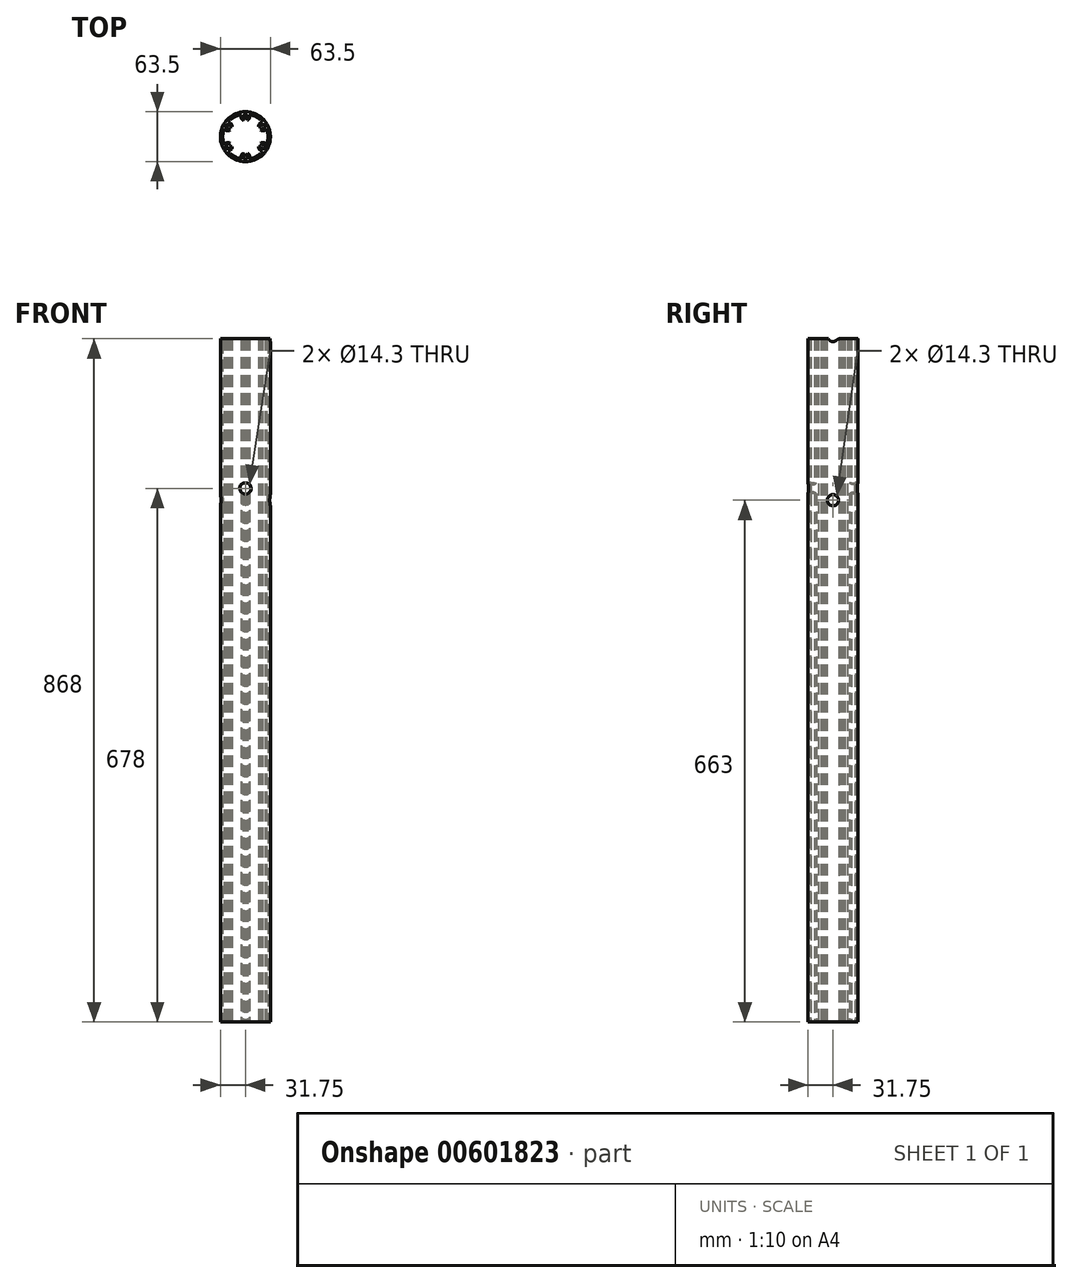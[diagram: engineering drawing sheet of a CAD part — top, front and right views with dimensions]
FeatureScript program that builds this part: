
annotation { "Feature Type Name" : "Feature", "Feature Type Description" : "" }
export const myFeature = defineFeature(function(context is Context, id is Id, definition is map)
    precondition{}
    {
        {
            var Q0;
            Q0=qCreatedBy(makeId("Top.planeOp"),FACE);
            var sketch = newSketch(context, id + "F0", { "sketchPlane" : qUnion([Q0])});
            skCircle(sketch, "E0", {"center": v(0, 0) * mm, "radius": 31.75 * mm});
            skCircle(sketch, "E1", {"center": v(0, 0) * mm, "radius": 28.75 * mm});
            skSolve(sketch);
        }
        {
            var Q0;
            Q0 = qSketchRegion(id + "F0", true);
            extrude(context, id + "F1", {"entities" : qUnion([Q0]), "depth" : 868 * mm, "offsetDistance" : 25 * mm});
        }
        {
            var Q0;
            Q0=qCreatedBy(makeId("Top.planeOp"),FACE);
            var sketch = newSketch(context, id + "F2", { "sketchPlane" : qUnion([Q0])});
            skCircle(sketch, "E2", {"center": v(0, 0) * mm, "radius": 25.75 * mm, "construction": true});
            skPoint(sketch, "E3", {"position": v(0, 25.75) * mm});
            skCircle(sketch, "E4", {"center": v(0, 25.75) * mm, "radius": 2.5 * mm});
            skCircle(sketch, "E5", {"center": v(0, 25.75) * mm, "radius": 5.5 * mm});
            skCircle(sketch, "E6.1.0", {"center": v(-22.3, 12.88) * mm, "radius": 5.5 * mm});
            skCircle(sketch, "E6.1.1", {"center": v(-22.3, 12.88) * mm, "radius": 2.5 * mm});
            skCircle(sketch, "E6.2.0", {"center": v(-22.3, -12.87) * mm, "radius": 5.5 * mm});
            skCircle(sketch, "E6.2.1", {"center": v(-22.3, -12.87) * mm, "radius": 2.5 * mm});
            skCircle(sketch, "E6.3.0", {"center": v(0, -25.75) * mm, "radius": 5.5 * mm});
            skCircle(sketch, "E6.3.1", {"center": v(0, -25.75) * mm, "radius": 2.5 * mm});
            skCircle(sketch, "E6.4.0", {"center": v(22.3, -12.88) * mm, "radius": 5.5 * mm});
            skCircle(sketch, "E6.4.1", {"center": v(22.3, -12.88) * mm, "radius": 2.5 * mm});
            skCircle(sketch, "E6.5.0", {"center": v(22.3, 12.88) * mm, "radius": 5.5 * mm});
            skCircle(sketch, "E6.5.1", {"center": v(22.3, 12.88) * mm, "radius": 2.5 * mm});
            skSolve(sketch);
        }
        {
            var Q0;
            Q0 = qSketchRegion(id + "F2", true);
            var Q1;
            Q1=makeQuery(id+"F1.opExtrude","CAP_FACE",FACE,{"disambiguationData":[OSD([sQuery(id+"F0.wireOp",EDGE,"E0"),sQuery(id+"F0.wireOp",EDGE,"E1")])],"isStart":false});
            extrude(context, id + "F3", {"entities" : qUnion([Q0]), "operationType" : NewBodyOperationType.ADD, "endBound" : BoundingType.UP_TO_SURFACE, "depth" : 25 * mm, "endBoundEntityFace" : qUnion([Q1]), "offsetDistance" : 25 * mm});
        }
        {
            var Q0;
            Q0=qCreatedBy(makeId("Top.planeOp"),FACE);
            var sketch = newSketch(context, id + "F4", { "sketchPlane" : qUnion([Q0])});
            skPoint(sketch, "E7", {"position": v(0, 25.75) * mm});
            skPoint(sketch, "E8", {"position": v(0, 20.25) * mm});
            skArc(sketch, "E9", {"start": v(-2.75, 20.99) * mm, "mid": v(0, 20.25) * mm, "end": v(2.75, 20.99) * mm});
            skLineSegment(sketch, "E10", {"start": v(0, 25.75) * mm, "end": v(-2.75, 20.99) * mm});
            skLineSegment(sketch, "E11", {"start": v(0, 25.75) * mm, "end": v(2.75, 20.99) * mm});
            skLineSegment(sketch, "E12.1.0", {"start": v(-22.3, 12.88) * mm, "end": v(-19.55, 8.11) * mm});
            skLineSegment(sketch, "E12.1.1", {"start": v(-22.3, 12.88) * mm, "end": v(-16.8, 12.88) * mm});
            skArc(sketch, "E12.1.2", {"start": v(-19.55, 8.11) * mm, "mid": v(-17.54, 10.13) * mm, "end": v(-16.8, 12.87) * mm});
            skLineSegment(sketch, "E12.2.0", {"start": v(-22.3, -12.87) * mm, "end": v(-16.8, -12.87) * mm});
            skLineSegment(sketch, "E12.2.1", {"start": v(-22.3, -12.87) * mm, "end": v(-19.55, -8.11) * mm});
            skArc(sketch, "E12.2.2", {"start": v(-16.8, -12.87) * mm, "mid": v(-17.54, -10.12) * mm, "end": v(-19.55, -8.11) * mm});
            skLineSegment(sketch, "E12.3.0", {"start": v(0, -25.75) * mm, "end": v(2.75, -20.99) * mm});
            skLineSegment(sketch, "E12.3.1", {"start": v(0, -25.75) * mm, "end": v(-2.75, -20.99) * mm});
            skArc(sketch, "E12.3.2", {"start": v(2.75, -20.99) * mm, "mid": v(0, -20.25) * mm, "end": v(-2.75, -20.99) * mm});
            skLineSegment(sketch, "E12.4.0", {"start": v(22.3, -12.88) * mm, "end": v(19.55, -8.11) * mm});
            skLineSegment(sketch, "E12.4.1", {"start": v(22.3, -12.88) * mm, "end": v(16.8, -12.88) * mm});
            skArc(sketch, "E12.4.2", {"start": v(19.55, -8.11) * mm, "mid": v(17.54, -10.13) * mm, "end": v(16.8, -12.88) * mm});
            skLineSegment(sketch, "E12.5.0", {"start": v(22.3, 12.88) * mm, "end": v(16.8, 12.87) * mm});
            skLineSegment(sketch, "E12.5.1", {"start": v(22.3, 12.88) * mm, "end": v(19.55, 8.11) * mm});
            skArc(sketch, "E12.5.2", {"start": v(16.8, 12.87) * mm, "mid": v(17.54, 10.13) * mm, "end": v(19.55, 8.11) * mm});
            skPoint(sketch, "E12.center", {"position": v(0, 0) * mm});
            skSolve(sketch);
        }
        {
            var Q0;
            Q0 = qSketchRegion(id + "F4", true);
            extrude(context, id + "F5", {"entities" : qUnion([Q0]), "operationType" : NewBodyOperationType.REMOVE, "endBound" : BoundingType.THROUGH_ALL, "depth" : 25 * mm, "offsetDistance" : 25 * mm});
        }
        {
            var Q0;
            Q0=qCreatedBy(makeId("Right.planeOp"),FACE);
            var sketch = newSketch(context, id + "F6", { "sketchPlane" : qUnion([Q0])});
            skPoint(sketch, "E13", {"position": v(0, 868) * mm});
            skLineSegment(sketch, "E14", {"start": v(-5.86, 868) * mm, "end": v(5.86, 868) * mm});
            skArc(sketch, "E15", {"start": v(-5.86, 868) * mm, "mid": v(0, 864.5) * mm, "end": v(5.86, 868) * mm});
            skPoint(sketch, "E16", {"position": v(0, 864.5) * mm});
            skSolve(sketch);
        }
        {
            var Q0;
            Q0 = qSketchRegion(id + "F6", true);
            extrude(context, id + "F7", {"entities" : qUnion([Q0]), "operationType" : NewBodyOperationType.REMOVE, "endBound" : BoundingType.THROUGH_ALL, "oppositeDirection" : true, "depth" : 25 * mm, "offsetDistance" : 25 * mm, "hasSecondDirection" : true, "secondDirectionBound" : SecondDirectionBoundingType.THROUGH_ALL, "secondDirectionOppositeDirection" : false, "secondDirectionDepth" : 25 * mm});
        }
        {
            var Q0;
            {var subQ0=sQuery(id+"F6.wireOp",EDGE,"E15");var subQ1=sQuery(id+"F6.wireOp",EDGE,"E14");Q0=makeQuery(id+"F7.boolean.opBoolean","COPY",EDGE,{"disambiguationData":[OD(0.0)],"derivedFrom":makeQuery(id+"F7.opExtrude","SWEPT_EDGE",EDGE,{"disambiguationData":[OSD([subQ1,subQ0]),TDD([makeQuery(id+"F6.imprint","INTERSECT",VERTEX,{"disambiguationData":[OD(0.0)],"derivedFrom":[subQ1,subQ0]})])]})});}
            var Q1;
            {var subQ0=sQuery(id+"F6.wireOp",EDGE,"E15");var subQ1=sQuery(id+"F6.wireOp",EDGE,"E14");Q1=makeQuery(id+"F7.boolean.opBoolean","COPY",EDGE,{"disambiguationData":[OD(0.0)],"derivedFrom":makeQuery(id+"F7.opExtrude","SWEPT_EDGE",EDGE,{"disambiguationData":[OSD([subQ1,subQ0]),TDD([makeQuery(id+"F6.imprint","INTERSECT",VERTEX,{"disambiguationData":[OD(1.0)],"derivedFrom":[subQ1,subQ0]})])]})});}
            var Q2;
            {var subQ0=sQuery(id+"F6.wireOp",EDGE,"E15");var subQ1=sQuery(id+"F6.wireOp",EDGE,"E14");Q2=makeQuery(id+"F7.boolean.opBoolean","COPY",EDGE,{"disambiguationData":[OD(1.0)],"derivedFrom":makeQuery(id+"F7.opExtrude","SWEPT_EDGE",EDGE,{"disambiguationData":[OSD([subQ1,subQ0]),TDD([makeQuery(id+"F6.imprint","INTERSECT",VERTEX,{"disambiguationData":[OD(1.0)],"derivedFrom":[subQ1,subQ0]})])]})});}
            var Q3;
            {var subQ0=sQuery(id+"F6.wireOp",EDGE,"E15");var subQ1=sQuery(id+"F6.wireOp",EDGE,"E14");Q3=makeQuery(id+"F7.boolean.opBoolean","COPY",EDGE,{"disambiguationData":[OD(1.0)],"derivedFrom":makeQuery(id+"F7.opExtrude","SWEPT_EDGE",EDGE,{"disambiguationData":[OSD([subQ1,subQ0]),TDD([makeQuery(id+"F6.imprint","INTERSECT",VERTEX,{"disambiguationData":[OD(0.0)],"derivedFrom":[subQ1,subQ0]})])]})});}
            fillet(context, id + "F8", {"entities" : qUnion([Q0, Q1, Q2, Q3]), "radius" : 6 * mm, "tangentPropagation" : true, "allowEdgeOverflow" : false});
        }
        {
            var Q0;
            Q0=qCreatedBy(makeId("Right.planeOp"),FACE);
            var sketch = newSketch(context, id + "F9", { "sketchPlane" : qUnion([Q0])});
            skCircle(sketch, "E17", {"center": v(0, 663) * mm, "radius": 7.15 * mm});
            skSolve(sketch);
        }
        {
            var Q0;
            Q0 = qSketchRegion(id + "F9", true);
            extrude(context, id + "F10", {"entities" : qUnion([Q0]), "operationType" : NewBodyOperationType.REMOVE, "endBound" : BoundingType.THROUGH_ALL, "oppositeDirection" : true, "depth" : 25 * mm, "offsetDistance" : 25 * mm, "hasSecondDirection" : true, "secondDirectionBound" : SecondDirectionBoundingType.THROUGH_ALL, "secondDirectionOppositeDirection" : false, "secondDirectionDepth" : 25 * mm});
        }
        {
            var Q0;
            Q0=qCreatedBy(makeId("Front.planeOp"),FACE);
            var sketch = newSketch(context, id + "F11", { "sketchPlane" : qUnion([Q0])});
            skCircle(sketch, "E18", {"center": v(0, 678) * mm, "radius": 7.15 * mm});
            skSolve(sketch);
        }
        {
            var Q0;
            Q0 = qSketchRegion(id + "F11", true);
            extrude(context, id + "F12", {"entities" : qUnion([Q0]), "operationType" : NewBodyOperationType.REMOVE, "endBound" : BoundingType.THROUGH_ALL, "oppositeDirection" : true, "depth" : 25 * mm, "offsetDistance" : 25 * mm, "hasSecondDirection" : true, "secondDirectionBound" : SecondDirectionBoundingType.THROUGH_ALL, "secondDirectionOppositeDirection" : false, "secondDirectionDepth" : 25 * mm});
        }
    });
